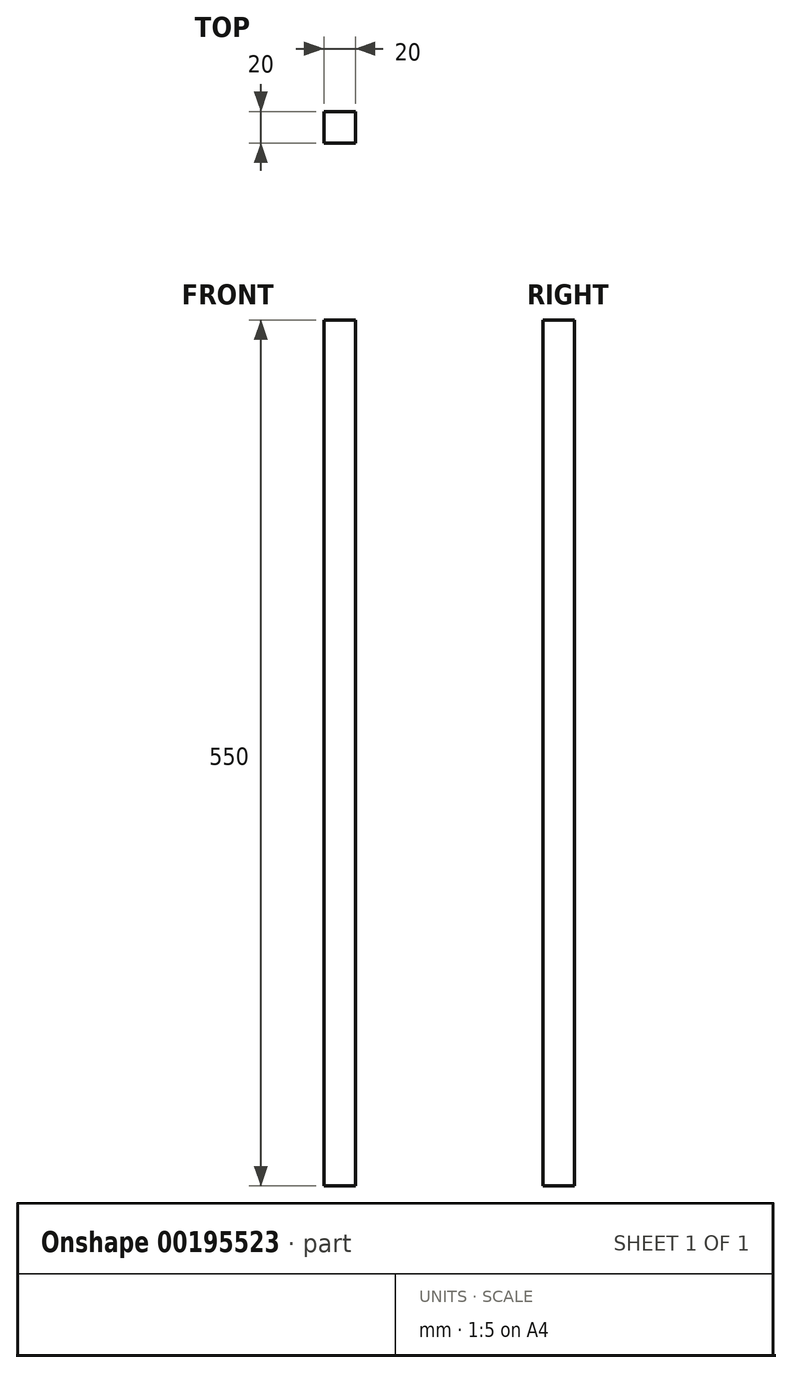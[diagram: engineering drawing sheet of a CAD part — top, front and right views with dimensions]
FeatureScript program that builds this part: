
annotation { "Feature Type Name" : "Feature", "Feature Type Description" : "" }
export const myFeature = defineFeature(function(context is Context, id is Id, definition is map)
    precondition{}
    {
        {
            var Q0;
            Q0=qCreatedBy(makeId("Top.planeOp"),FACE);
            var sketch = newSketch(context, id + "F0", { "sketchPlane" : qUnion([Q0])});
            skLineSegment(sketch, "E0.bottom", {"start": v(-96.3, -36.6) * mm, "end": v(-76.3, -36.6) * mm});
            skLineSegment(sketch, "E0.top", {"start": v(-96.3, -16.6) * mm, "end": v(-76.3, -16.6) * mm});
            skLineSegment(sketch, "E0.left", {"start": v(-96.3, -36.6) * mm, "end": v(-96.3, -16.6) * mm});
            skLineSegment(sketch, "E0.right", {"start": v(-76.3, -36.6) * mm, "end": v(-76.3, -16.6) * mm});
            skSolve(sketch);
        }
        {
            var Q0;
            Q0=makeQuery(id+"F0.imprint","IMPRINT",FACE,{"disambiguationData":[TD([[makeQuery(id+"F0.imprint","IMPRINT",EDGE,{"derivedFrom":sQuery(id+"F0.wireOp",EDGE,"E0.bottom")}),1.0]])]});
            extrude(context, id + "F1", {"entities" : qUnion([Q0]), "depth" : 550 * mm});
        }
    });
